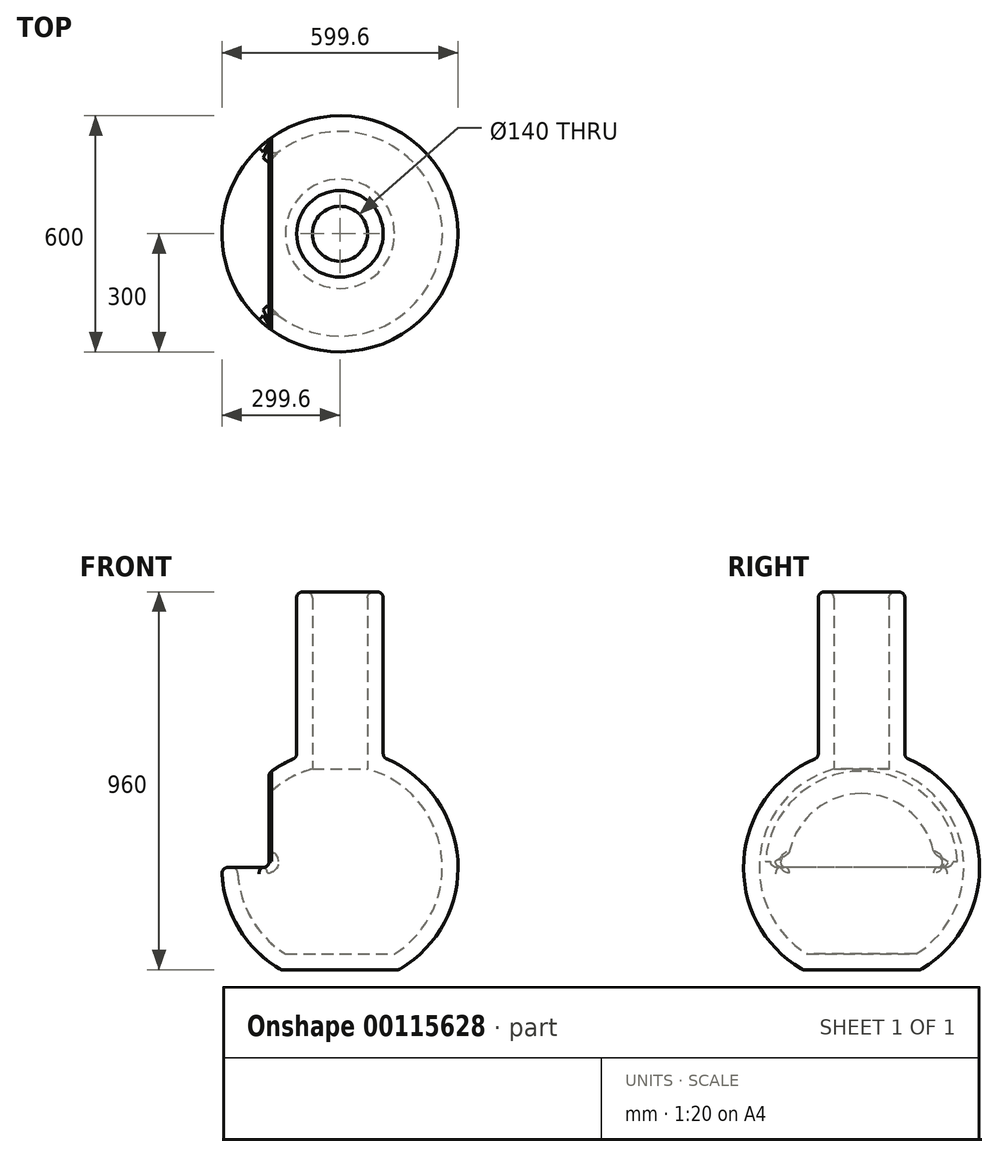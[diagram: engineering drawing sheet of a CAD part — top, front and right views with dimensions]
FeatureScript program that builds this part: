
annotation { "Feature Type Name" : "Feature", "Feature Type Description" : "" }
export const myFeature = defineFeature(function(context is Context, id is Id, definition is map)
    precondition{}
    {
        {
            var Q0;
            Q0=qCreatedBy(makeId("Front.planeOp"),FACE);
            var sketch = newSketch(context, id + "F0", { "sketchPlane" : qUnion([Q0])});
            skArc(sketch, "E0", {"start": v(0, 300) * mm, "mid": v(-254.47, 158.89) * mm, "end": v(-269.55, -131.7) * mm});
            skLineSegment(sketch, "E1", {"start": v(0, -260) * mm, "end": v(0, 700) * mm});
            skLineSegment(sketch, "E2", {"start": v(0, 700) * mm, "end": v(-110, 700) * mm});
            skLineSegment(sketch, "E3", {"start": v(-110, 700) * mm, "end": v(-110, 279.1) * mm});
            skLineSegment(sketch, "E4", {"start": v(0, 0) * mm, "end": v(-300, 0) * mm});
            skLineSegment(sketch, "E5", {"start": v(0, -260) * mm, "end": v(-149.67, -260) * mm});
            skLineSegment(sketch, "E6.MirrorCS", {"start": v(0, 260) * mm, "end": v(-149.67, 260) * mm});
            skLineSegment(sketch, "E7", {"start": v(0, -131.7) * mm, "end": v(-269.55, -131.7) * mm});
            skLineSegment(sketch, "E8", {"start": v(-180, 240) * mm, "end": v(-180, 0) * mm});
            skLineSegment(sketch, "E9", {"start": v(-180, 240) * mm, "end": v(0, 240) * mm});
            skArc(sketch, "E10", {"start": v(-269.55, -131.7) * mm, "mid": v(-219.2, -204.82) * mm, "end": v(-149.67, -260) * mm});
            skLineSegment(sketch, "E11", {"start": v(-269.55, -131.7) * mm, "end": v(-269.55, -131.7) * mm});
            skLineSegment(sketch, "E12", {"start": v(0, 131.7) * mm, "end": v(-269.55, 131.7) * mm});
            skSolve(sketch);
        }
        {
            var Q0;
            {var subQ0=sQuery(id+"F0.wireOp",EDGE,"E4");var subQ1=sQuery(id+"F0.wireOp",EDGE,"E0");var subQ2=makeQuery(id+"F0.imprint","INTERSECT",VERTEX,{"derivedFrom":[subQ1,subQ0]});Q0=makeQuery(id+"F0.imprint","IMPRINT",FACE,{"disambiguationData":[TD([[makeQuery(id+"F0.imprint","IMPRINT",EDGE,{"disambiguationData":[TD([[subQ2,1.0]])],"derivedFrom":subQ0}),-1.0]])]});}
            var Q1;
            {var subQ6=sQuery(id+"F0.wireOp",EDGE,"E7");Q1=makeQuery(id+"F0.imprint","IMPRINT",FACE,{"disambiguationData":[TD([[makeQuery(id+"F0.imprint","IMPRINT",EDGE,{"derivedFrom":subQ6}),-1.0]])]});}
            var Q2;
            {var subQ0=sQuery(id+"F0.wireOp",EDGE,"E5");Q2=makeQuery(id+"F0.imprint","IMPRINT",FACE,{"disambiguationData":[TD([[makeQuery(id+"F0.imprint","IMPRINT",EDGE,{"derivedFrom":subQ0}),-1.0]])]});}
            var Q3;
            {var subQ0=sQuery(id+"F0.wireOp",EDGE,"E6.MirrorCS");Q3=makeQuery(id+"F0.imprint","IMPRINT",FACE,{"disambiguationData":[TD([[makeQuery(id+"F0.imprint","IMPRINT",EDGE,{"derivedFrom":subQ0}),1.0]])]});}
            var Q4;
            {var subQ4=sQuery(id+"F0.wireOp",EDGE,"E6.MirrorCS");Q4=makeQuery(id+"F0.imprint","IMPRINT",FACE,{"disambiguationData":[TD([[makeQuery(id+"F0.imprint","IMPRINT",EDGE,{"derivedFrom":subQ4}),-1.0]])]});}
            var Q5;
            {var subQ4=sQuery(id+"F0.wireOp",EDGE,"E2");Q5=makeQuery(id+"F0.imprint","IMPRINT",FACE,{"disambiguationData":[TD([[makeQuery(id+"F0.imprint","IMPRINT",EDGE,{"derivedFrom":subQ4}),1.0]])]});}
            var Q6;
            {var subQ0=sQuery(id+"F0.wireOp",EDGE,"E9");Q6=makeQuery(id+"F0.imprint","IMPRINT",FACE,{"disambiguationData":[TD([[makeQuery(id+"F0.imprint","IMPRINT",EDGE,{"derivedFrom":subQ0}),-1.0]])]});}
            var Q7;
            {var subQ1=sQuery(id+"F0.wireOp",EDGE,"E0");var subQ3=sQuery(id+"F0.wireOp",EDGE,"E12");var subQ4=makeQuery(id+"F0.imprint","INTERSECT",VERTEX,{"derivedFrom":[subQ1,subQ3]});Q7=makeQuery(id+"F0.imprint","IMPRINT",FACE,{"disambiguationData":[TD([[makeQuery(id+"F0.imprint","IMPRINT",EDGE,{"disambiguationData":[TD([[subQ4,1.0]])],"derivedFrom":subQ3}),-1.0]])]});}
            var Q8;
            {var subQ0=sQuery(id+"F0.wireOp",EDGE,"E4");var subQ1=sQuery(id+"F0.wireOp",EDGE,"E1");var subQ2=makeQuery(id+"F0.imprint","INTERSECT",VERTEX,{"derivedFrom":[subQ1,subQ0]});Q8=makeQuery(id+"F0.imprint","IMPRINT",FACE,{"disambiguationData":[TD([[makeQuery(id+"F0.imprint","IMPRINT",EDGE,{"disambiguationData":[TD([[subQ2,-1.0]])],"derivedFrom":subQ1}),1.0]])]});}
            var Q9;
            Q9=sQuery(id+"F0.wireOp",EDGE,"E1");
            revolve(context, id + "F1", {"entities" : qUnion([Q0, Q1, Q2, Q3, Q4, Q5, Q6, Q7, Q8]), "axis" : qUnion([Q9]), "revolveType" : RevolveType.FULL});
        }
        {
            var Q0;
            Q0=makeQuery(id+"F1.opRevolve","CAP_FACE",FACE,{"disambiguationData":[OSD([sQuery(id+"F0.wireOp",EDGE,"E0"),sQuery(id+"F0.wireOp",EDGE,"E1"),sQuery(id+"F0.wireOp",EDGE,"E2"),sQuery(id+"F0.wireOp",EDGE,"E3"),sQuery(id+"F0.wireOp",EDGE,"E5"),sQuery(id+"F0.wireOp",EDGE,"E10")])],"isStart":false});
            var Q1;
            Q1=makeQuery(id+"F1.opRevolve","CAP_FACE",FACE,{"disambiguationData":[OSD([sQuery(id+"F0.wireOp",EDGE,"E0"),sQuery(id+"F0.wireOp",EDGE,"E1"),sQuery(id+"F0.wireOp",EDGE,"E2"),sQuery(id+"F0.wireOp",EDGE,"E3"),sQuery(id+"F0.wireOp",EDGE,"E5"),sQuery(id+"F0.wireOp",EDGE,"E10")])],"isStart":true});
            var Q2;
            Q2=makeQuery(id+"F1.opRevolve","SWEPT_FACE",FACE,{"disambiguationData":[OSD([sQuery(id+"F0.wireOp",EDGE,"E2")])]});
            shell(context, id + "F2", {"entities" : qUnion([Q0, Q1, Q2]), "thickness" : 40 * mm});
        }
        {
            var Q0;
            {var subQ0=sQuery(id+"F0.wireOp",EDGE,"E4");var subQ1=sQuery(id+"F0.wireOp",EDGE,"E0");var subQ2=makeQuery(id+"F0.imprint","INTERSECT",VERTEX,{"derivedFrom":[subQ1,subQ0]});Q0=makeQuery(id+"F0.imprint","IMPRINT",FACE,{"disambiguationData":[TD([[makeQuery(id+"F0.imprint","IMPRINT",EDGE,{"disambiguationData":[TD([[subQ2,1.0]])],"derivedFrom":subQ1}),1.0]])]});}
            var Q1;
            {var subQ1=sQuery(id+"F0.wireOp",EDGE,"E0");var subQ3=sQuery(id+"F0.wireOp",EDGE,"E12");var subQ4=makeQuery(id+"F0.imprint","INTERSECT",VERTEX,{"derivedFrom":[subQ1,subQ3]});Q1=makeQuery(id+"F0.imprint","IMPRINT",FACE,{"disambiguationData":[TD([[makeQuery(id+"F0.imprint","IMPRINT",EDGE,{"disambiguationData":[TD([[subQ4,1.0]])],"derivedFrom":subQ3}),-1.0]])]});}
            extrude(context, id + "F3", {"entities" : qUnion([Q0, Q1]), "operationType" : NewBodyOperationType.REMOVE, "endBound" : BoundingType.THROUGH_ALL, "oppositeDirection" : true, "depth" : 25 * mm, "hasSecondDirection" : true, "secondDirectionOppositeDirection" : false, "secondDirectionDepth" : 239.89 * mm});
        }
        {
            var Q0;
            Q0=makeQuery(id+"F3.boolean.opBoolean","COPY",FACE,{"derivedFrom":makeQuery(id+"F3.opExtrude","SWEPT_FACE",FACE,{"disambiguationData":[OSD([sQuery(id+"F0.wireOp",EDGE,"E4")])]})});
            var Q1;
            Q1=makeQuery(id+"F1.opRevolve","SWEPT_FACE",FACE,{"disambiguationData":[OSD([sQuery(id+"F0.wireOp",EDGE,"E0"),sQuery(id+"F0.wireOp",EDGE,"E10")])]});
            fillet(context, id + "F4", {"entities" : qUnion([Q0, Q1]), "radius" : 15 * mm, "tangentPropagation" : true, "allowEdgeOverflow" : false});
        }
        {
            var Q0;
            Q0=makeQuery(id+"F1.opRevolve","SWEPT_FACE",FACE,{"disambiguationData":[OSD([sQuery(id+"F0.wireOp",EDGE,"E2")])]});
            fillet(context, id + "F5", {"entities" : qUnion([Q0]), "radius" : 15 * mm, "tangentPropagation" : true, "allowEdgeOverflow" : false});
        }
    });
